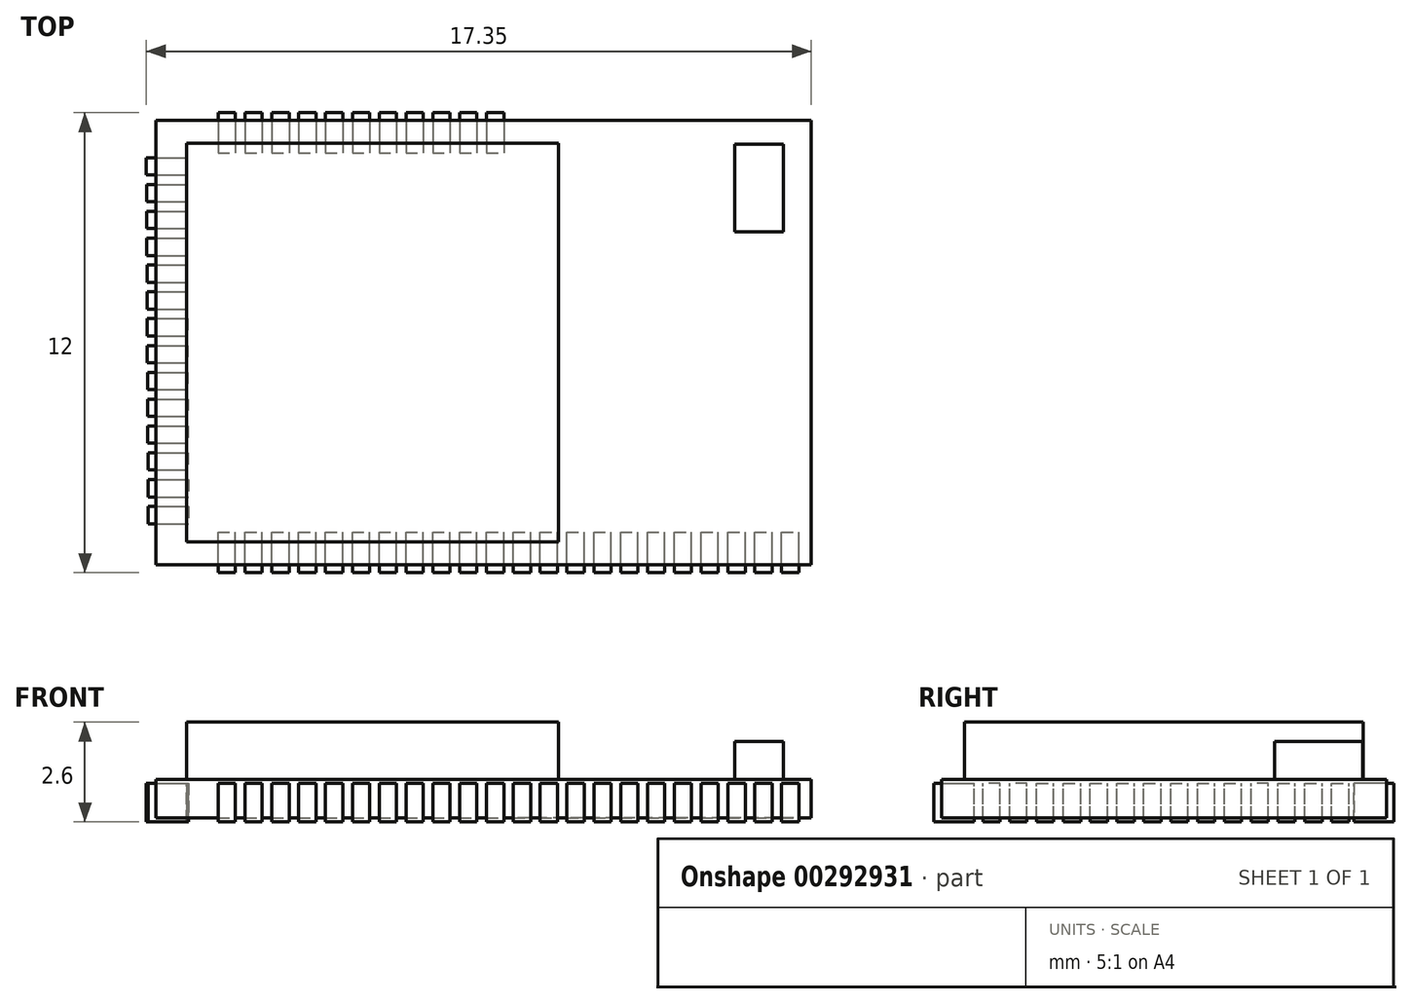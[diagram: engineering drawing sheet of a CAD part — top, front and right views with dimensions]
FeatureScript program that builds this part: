
annotation { "Feature Type Name" : "Feature", "Feature Type Description" : "" }
export const myFeature = defineFeature(function(context is Context, id is Id, definition is map)
    precondition{}
    {
        {
            var Q0;
            Q0=qCreatedBy(makeId("Top.planeOp"),FACE);
            var sketch = newSketch(context, id + "F0", { "sketchPlane" : qUnion([Q0])});
            skLineSegment(sketch, "E0.bottom", {"start": v(8.55, -5.8) * mm, "end": v(-8.55, -5.8) * mm});
            skLineSegment(sketch, "E0.top", {"start": v(8.55, 5.8) * mm, "end": v(-8.55, 5.8) * mm});
            skLineSegment(sketch, "E0.left", {"start": v(8.55, -5.8) * mm, "end": v(8.55, 5.8) * mm});
            skLineSegment(sketch, "E0.right", {"start": v(-8.55, -5.8) * mm, "end": v(-8.55, 5.8) * mm});
            skPoint(sketch, "E0.middle", {"position": v(0, 0) * mm});
            skLineSegment(sketch, "E1.bottom", {"start": v(1.95, -5.2) * mm, "end": v(-7.75, -5.2) * mm});
            skLineSegment(sketch, "E1.top", {"start": v(1.95, 5.2) * mm, "end": v(-7.75, 5.2) * mm});
            skLineSegment(sketch, "E1.left", {"start": v(1.95, -5.2) * mm, "end": v(1.95, 5.2) * mm});
            skLineSegment(sketch, "E1.right", {"start": v(-7.75, -5.2) * mm, "end": v(-7.75, 5.2) * mm});
            skPoint(sketch, "E1.middle", {"position": v(-2.9, 0) * mm});
            skLineSegment(sketch, "E2.bottom", {"start": v(7.82, 2.89) * mm, "end": v(6.55, 2.89) * mm});
            skLineSegment(sketch, "E2.top", {"start": v(7.82, 5.18) * mm, "end": v(6.55, 5.18) * mm});
            skLineSegment(sketch, "E2.left", {"start": v(7.82, 2.89) * mm, "end": v(7.82, 5.18) * mm});
            skLineSegment(sketch, "E2.right", {"start": v(6.55, 2.89) * mm, "end": v(6.55, 5.18) * mm});
            skPoint(sketch, "E2.middle", {"position": v(7.18, 4.03) * mm});
            skSolve(sketch);
        }
        {
            var Q0;
            Q0=makeQuery(id+"F0.imprint","IMPRINT",FACE,{"disambiguationData":[TD([[makeQuery(id+"F0.imprint","IMPRINT",EDGE,{"derivedFrom":sQuery(id+"F0.wireOp",EDGE,"E0.bottom")}),-1.0]])]});
            var Q1;
            Q1=makeQuery(id+"F0.imprint","IMPRINT",FACE,{"disambiguationData":[TD([[makeQuery(id+"F0.imprint","IMPRINT",EDGE,{"derivedFrom":sQuery(id+"F0.wireOp",EDGE,"E1.bottom")}),-1.0]])]});
            var Q2;
            Q2=makeQuery(id+"F0.imprint","IMPRINT",FACE,{"disambiguationData":[TD([[makeQuery(id+"F0.imprint","IMPRINT",EDGE,{"derivedFrom":sQuery(id+"F0.wireOp",EDGE,"E2.bottom")}),-1.0]])]});
            extrude(context, id + "F1", {"entities" : qUnion([Q0, Q1, Q2]), "oppositeDirection" : true, "depth" : 1 * mm});
        }
        {
            var Q0;
            Q0=makeQuery(id+"F0.imprint","IMPRINT",FACE,{"disambiguationData":[TD([[makeQuery(id+"F0.imprint","IMPRINT",EDGE,{"derivedFrom":sQuery(id+"F0.wireOp",EDGE,"E1.bottom")}),-1.0]])]});
            extrude(context, id + "F2", {"entities" : qUnion([Q0]), "depth" : 1.5 * mm});
        }
        {
            var Q0;
            Q0=makeQuery(id+"F0.imprint","IMPRINT",FACE,{"disambiguationData":[TD([[makeQuery(id+"F0.imprint","IMPRINT",EDGE,{"derivedFrom":sQuery(id+"F0.wireOp",EDGE,"E2.bottom")}),-1.0]])]});
            extrude(context, id + "F3", {"entities" : qUnion([Q0]), "depth" : 1 * mm});
        }
        {
            var Q0;
            Q0=makeQuery(id+"F1.opExtrude","CAP_FACE",FACE,{"disambiguationData":[OSD([sQuery(id+"F0.wireOp",EDGE,"E0.bottom"),sQuery(id+"F0.wireOp",EDGE,"E0.top"),sQuery(id+"F0.wireOp",EDGE,"E0.left"),sQuery(id+"F0.wireOp",EDGE,"E0.right")])],"isStart":false});
            var sketch = newSketch(context, id + "F4", { "sketchPlane" : qUnion([Q0])});
            skLineSegment(sketch, "E3.bottom", {"start": v(7.78, 6) * mm, "end": v(8.22, 6) * mm});
            skLineSegment(sketch, "E3.top", {"start": v(7.78, 4.95) * mm, "end": v(8.23, 4.95) * mm});
            skLineSegment(sketch, "E3.left", {"start": v(7.78, 6) * mm, "end": v(7.78, 4.95) * mm});
            skLineSegment(sketch, "E3.right", {"start": v(8.23, 6) * mm, "end": v(8.23, 4.95) * mm});
            skPoint(sketch, "E3.middle", {"position": v(8, 5.47) * mm});
            skPoint(sketch, "E4", {"position": v(8, 6) * mm});
            skLineSegment(sketch, "E5.1.0.0", {"start": v(7.53, 6) * mm, "end": v(7.53, 4.95) * mm});
            skLineSegment(sketch, "E5.1.0.1", {"start": v(7.08, 6) * mm, "end": v(7.08, 4.95) * mm});
            skLineSegment(sketch, "E5.1.0.2", {"start": v(7.08, 4.95) * mm, "end": v(7.53, 4.95) * mm});
            skLineSegment(sketch, "E5.1.0.3", {"start": v(7.08, 6) * mm, "end": v(7.52, 6) * mm});
            skPoint(sketch, "E5.1.0.4", {"position": v(7.3, 6) * mm});
            skPoint(sketch, "E5.1.0.5", {"position": v(7.3, 5.47) * mm});
            skLineSegment(sketch, "E5.2.0.0", {"start": v(6.83, 6) * mm, "end": v(6.83, 4.95) * mm});
            skLineSegment(sketch, "E5.2.0.1", {"start": v(6.38, 6) * mm, "end": v(6.38, 4.95) * mm});
            skLineSegment(sketch, "E5.2.0.2", {"start": v(6.38, 4.95) * mm, "end": v(6.83, 4.95) * mm});
            skLineSegment(sketch, "E5.2.0.3", {"start": v(6.38, 6) * mm, "end": v(6.82, 6) * mm});
            skPoint(sketch, "E5.2.0.4", {"position": v(6.6, 6) * mm});
            skPoint(sketch, "E5.2.0.5", {"position": v(6.6, 5.47) * mm});
            skLineSegment(sketch, "E5.3.0.0", {"start": v(6.13, 6) * mm, "end": v(6.13, 4.95) * mm});
            skLineSegment(sketch, "E5.3.0.1", {"start": v(5.68, 6) * mm, "end": v(5.68, 4.95) * mm});
            skLineSegment(sketch, "E5.3.0.2", {"start": v(5.68, 4.95) * mm, "end": v(6.13, 4.95) * mm});
            skLineSegment(sketch, "E5.3.0.3", {"start": v(5.68, 6) * mm, "end": v(6.12, 6) * mm});
            skPoint(sketch, "E5.3.0.4", {"position": v(5.9, 6) * mm});
            skPoint(sketch, "E5.3.0.5", {"position": v(5.9, 5.47) * mm});
            skLineSegment(sketch, "E5.4.0.0", {"start": v(5.43, 6) * mm, "end": v(5.43, 4.95) * mm});
            skLineSegment(sketch, "E5.4.0.1", {"start": v(4.98, 6) * mm, "end": v(4.98, 4.95) * mm});
            skLineSegment(sketch, "E5.4.0.2", {"start": v(4.98, 4.95) * mm, "end": v(5.43, 4.95) * mm});
            skLineSegment(sketch, "E5.4.0.3", {"start": v(4.98, 6) * mm, "end": v(5.42, 6) * mm});
            skPoint(sketch, "E5.4.0.4", {"position": v(5.2, 6) * mm});
            skPoint(sketch, "E5.4.0.5", {"position": v(5.2, 5.47) * mm});
            skLineSegment(sketch, "E5.5.0.0", {"start": v(4.73, 6) * mm, "end": v(4.73, 4.95) * mm});
            skLineSegment(sketch, "E5.5.0.1", {"start": v(4.28, 6) * mm, "end": v(4.28, 4.95) * mm});
            skLineSegment(sketch, "E5.5.0.2", {"start": v(4.28, 4.95) * mm, "end": v(4.73, 4.95) * mm});
            skLineSegment(sketch, "E5.5.0.3", {"start": v(4.28, 6) * mm, "end": v(4.72, 6) * mm});
            skPoint(sketch, "E5.5.0.4", {"position": v(4.5, 6) * mm});
            skPoint(sketch, "E5.5.0.5", {"position": v(4.5, 5.47) * mm});
            skLineSegment(sketch, "E5.6.0.0", {"start": v(4.03, 6) * mm, "end": v(4.03, 4.95) * mm});
            skLineSegment(sketch, "E5.6.0.1", {"start": v(3.58, 6) * mm, "end": v(3.58, 4.95) * mm});
            skLineSegment(sketch, "E5.6.0.2", {"start": v(3.58, 4.95) * mm, "end": v(4.03, 4.95) * mm});
            skLineSegment(sketch, "E5.6.0.3", {"start": v(3.58, 6) * mm, "end": v(4.02, 6) * mm});
            skPoint(sketch, "E5.6.0.4", {"position": v(3.8, 6) * mm});
            skPoint(sketch, "E5.6.0.5", {"position": v(3.8, 5.47) * mm});
            skLineSegment(sketch, "E5.7.0.0", {"start": v(3.33, 6) * mm, "end": v(3.33, 4.95) * mm});
            skLineSegment(sketch, "E5.7.0.1", {"start": v(2.88, 6) * mm, "end": v(2.88, 4.95) * mm});
            skLineSegment(sketch, "E5.7.0.2", {"start": v(2.88, 4.95) * mm, "end": v(3.33, 4.95) * mm});
            skLineSegment(sketch, "E5.7.0.3", {"start": v(2.88, 6) * mm, "end": v(3.32, 6) * mm});
            skPoint(sketch, "E5.7.0.4", {"position": v(3.1, 6) * mm});
            skPoint(sketch, "E5.7.0.5", {"position": v(3.1, 5.47) * mm});
            skLineSegment(sketch, "E5.8.0.0", {"start": v(2.63, 6) * mm, "end": v(2.63, 4.95) * mm});
            skLineSegment(sketch, "E5.8.0.1", {"start": v(2.18, 6) * mm, "end": v(2.18, 4.95) * mm});
            skLineSegment(sketch, "E5.8.0.2", {"start": v(2.18, 4.95) * mm, "end": v(2.63, 4.95) * mm});
            skLineSegment(sketch, "E5.8.0.3", {"start": v(2.18, 6) * mm, "end": v(2.62, 6) * mm});
            skPoint(sketch, "E5.8.0.4", {"position": v(2.4, 6) * mm});
            skPoint(sketch, "E5.8.0.5", {"position": v(2.4, 5.47) * mm});
            skLineSegment(sketch, "E5.9.0.0", {"start": v(1.93, 6) * mm, "end": v(1.93, 4.95) * mm});
            skLineSegment(sketch, "E5.9.0.1", {"start": v(1.48, 6) * mm, "end": v(1.48, 4.95) * mm});
            skLineSegment(sketch, "E5.9.0.2", {"start": v(1.48, 4.95) * mm, "end": v(1.93, 4.95) * mm});
            skLineSegment(sketch, "E5.9.0.3", {"start": v(1.48, 6) * mm, "end": v(1.92, 6) * mm});
            skPoint(sketch, "E5.9.0.4", {"position": v(1.7, 6) * mm});
            skPoint(sketch, "E5.9.0.5", {"position": v(1.7, 5.47) * mm});
            skLineSegment(sketch, "E5.10.0.0", {"start": v(1.23, 6) * mm, "end": v(1.23, 4.95) * mm});
            skLineSegment(sketch, "E5.10.0.1", {"start": v(0.78, 6) * mm, "end": v(0.78, 4.95) * mm});
            skLineSegment(sketch, "E5.10.0.2", {"start": v(0.78, 4.95) * mm, "end": v(1.23, 4.95) * mm});
            skLineSegment(sketch, "E5.10.0.3", {"start": v(0.78, 6) * mm, "end": v(1.22, 6) * mm});
            skPoint(sketch, "E5.10.0.4", {"position": v(1, 6) * mm});
            skPoint(sketch, "E5.10.0.5", {"position": v(1, 5.47) * mm});
            skLineSegment(sketch, "E5.11.0.0", {"start": v(0.53, 6) * mm, "end": v(0.53, 4.95) * mm});
            skLineSegment(sketch, "E5.11.0.1", {"start": v(0.08, 6) * mm, "end": v(0.08, 4.95) * mm});
            skLineSegment(sketch, "E5.11.0.2", {"start": v(0.08, 4.95) * mm, "end": v(0.53, 4.95) * mm});
            skLineSegment(sketch, "E5.11.0.3", {"start": v(0.08, 6) * mm, "end": v(0.52, 6) * mm});
            skPoint(sketch, "E5.11.0.4", {"position": v(0.3, 6) * mm});
            skPoint(sketch, "E5.11.0.5", {"position": v(0.3, 5.47) * mm});
            skLineSegment(sketch, "E5.12.0.0", {"start": v(-0.17, 6) * mm, "end": v(-0.17, 4.95) * mm});
            skLineSegment(sketch, "E5.12.0.1", {"start": v(-0.62, 6) * mm, "end": v(-0.62, 4.95) * mm});
            skLineSegment(sketch, "E5.12.0.2", {"start": v(-0.62, 4.95) * mm, "end": v(-0.17, 4.95) * mm});
            skLineSegment(sketch, "E5.12.0.3", {"start": v(-0.62, 6) * mm, "end": v(-0.18, 6) * mm});
            skPoint(sketch, "E5.12.0.4", {"position": v(-0.4, 6) * mm});
            skPoint(sketch, "E5.12.0.5", {"position": v(-0.4, 5.47) * mm});
            skLineSegment(sketch, "E5.13.0.0", {"start": v(-0.87, 6) * mm, "end": v(-0.87, 4.95) * mm});
            skLineSegment(sketch, "E5.13.0.1", {"start": v(-1.32, 6) * mm, "end": v(-1.32, 4.95) * mm});
            skLineSegment(sketch, "E5.13.0.2", {"start": v(-1.32, 4.95) * mm, "end": v(-0.87, 4.95) * mm});
            skLineSegment(sketch, "E5.13.0.3", {"start": v(-1.32, 6) * mm, "end": v(-0.88, 6) * mm});
            skPoint(sketch, "E5.13.0.4", {"position": v(-1.1, 6) * mm});
            skPoint(sketch, "E5.13.0.5", {"position": v(-1.1, 5.47) * mm});
            skLineSegment(sketch, "E5.14.0.0", {"start": v(-1.57, 6) * mm, "end": v(-1.57, 4.95) * mm});
            skLineSegment(sketch, "E5.14.0.1", {"start": v(-2.02, 6) * mm, "end": v(-2.02, 4.95) * mm});
            skLineSegment(sketch, "E5.14.0.2", {"start": v(-2.02, 4.95) * mm, "end": v(-1.57, 4.95) * mm});
            skLineSegment(sketch, "E5.14.0.3", {"start": v(-2.02, 6) * mm, "end": v(-1.58, 6) * mm});
            skPoint(sketch, "E5.14.0.4", {"position": v(-1.8, 6) * mm});
            skPoint(sketch, "E5.14.0.5", {"position": v(-1.8, 5.47) * mm});
            skLineSegment(sketch, "E5.15.0.0", {"start": v(-2.27, 6) * mm, "end": v(-2.27, 4.95) * mm});
            skLineSegment(sketch, "E5.15.0.1", {"start": v(-2.73, 6) * mm, "end": v(-2.73, 4.95) * mm});
            skLineSegment(sketch, "E5.15.0.2", {"start": v(-2.72, 4.95) * mm, "end": v(-2.28, 4.95) * mm});
            skLineSegment(sketch, "E5.15.0.3", {"start": v(-2.72, 6) * mm, "end": v(-2.28, 6) * mm});
            skPoint(sketch, "E5.15.0.4", {"position": v(-2.5, 6) * mm});
            skPoint(sketch, "E5.15.0.5", {"position": v(-2.5, 5.47) * mm});
            skLineSegment(sketch, "E5.16.0.0", {"start": v(-2.97, 6) * mm, "end": v(-2.97, 4.95) * mm});
            skLineSegment(sketch, "E5.16.0.1", {"start": v(-3.43, 6) * mm, "end": v(-3.43, 4.95) * mm});
            skLineSegment(sketch, "E5.16.0.2", {"start": v(-3.42, 4.95) * mm, "end": v(-2.98, 4.95) * mm});
            skLineSegment(sketch, "E5.16.0.3", {"start": v(-3.42, 6) * mm, "end": v(-2.98, 6) * mm});
            skPoint(sketch, "E5.16.0.4", {"position": v(-3.2, 6) * mm});
            skPoint(sketch, "E5.16.0.5", {"position": v(-3.2, 5.47) * mm});
            skLineSegment(sketch, "E5.17.0.0", {"start": v(-3.67, 6) * mm, "end": v(-3.67, 4.95) * mm});
            skLineSegment(sketch, "E5.17.0.1", {"start": v(-4.12, 6) * mm, "end": v(-4.12, 4.95) * mm});
            skLineSegment(sketch, "E5.17.0.2", {"start": v(-4.12, 4.95) * mm, "end": v(-3.67, 4.95) * mm});
            skLineSegment(sketch, "E5.17.0.3", {"start": v(-4.12, 6) * mm, "end": v(-3.68, 6) * mm});
            skPoint(sketch, "E5.17.0.4", {"position": v(-3.9, 6) * mm});
            skPoint(sketch, "E5.17.0.5", {"position": v(-3.9, 5.47) * mm});
            skLineSegment(sketch, "E5.18.0.0", {"start": v(-4.37, 6) * mm, "end": v(-4.37, 4.95) * mm});
            skLineSegment(sketch, "E5.18.0.1", {"start": v(-4.83, 6) * mm, "end": v(-4.83, 4.95) * mm});
            skLineSegment(sketch, "E5.18.0.2", {"start": v(-4.82, 4.95) * mm, "end": v(-4.38, 4.95) * mm});
            skLineSegment(sketch, "E5.18.0.3", {"start": v(-4.82, 6) * mm, "end": v(-4.38, 6) * mm});
            skPoint(sketch, "E5.18.0.4", {"position": v(-4.6, 6) * mm});
            skPoint(sketch, "E5.18.0.5", {"position": v(-4.6, 5.47) * mm});
            skLineSegment(sketch, "E5.19.0.0", {"start": v(-5.07, 6) * mm, "end": v(-5.07, 4.95) * mm});
            skLineSegment(sketch, "E5.19.0.1", {"start": v(-5.53, 6) * mm, "end": v(-5.53, 4.95) * mm});
            skLineSegment(sketch, "E5.19.0.2", {"start": v(-5.52, 4.95) * mm, "end": v(-5.08, 4.95) * mm});
            skLineSegment(sketch, "E5.19.0.3", {"start": v(-5.52, 6) * mm, "end": v(-5.08, 6) * mm});
            skPoint(sketch, "E5.19.0.4", {"position": v(-5.3, 6) * mm});
            skPoint(sketch, "E5.19.0.5", {"position": v(-5.3, 5.47) * mm});
            skLineSegment(sketch, "E5.20.0.0", {"start": v(-5.77, 6) * mm, "end": v(-5.77, 4.95) * mm});
            skLineSegment(sketch, "E5.20.0.1", {"start": v(-6.23, 6) * mm, "end": v(-6.23, 4.95) * mm});
            skLineSegment(sketch, "E5.20.0.2", {"start": v(-6.22, 4.95) * mm, "end": v(-5.78, 4.95) * mm});
            skLineSegment(sketch, "E5.20.0.3", {"start": v(-6.22, 6) * mm, "end": v(-5.78, 6) * mm});
            skPoint(sketch, "E5.20.0.4", {"position": v(-6, 6) * mm});
            skPoint(sketch, "E5.20.0.5", {"position": v(-6, 5.47) * mm});
            skLineSegment(sketch, "E5.21.0.0", {"start": v(-6.47, 6) * mm, "end": v(-6.47, 4.95) * mm});
            skLineSegment(sketch, "E5.21.0.1", {"start": v(-6.92, 6) * mm, "end": v(-6.92, 4.95) * mm});
            skLineSegment(sketch, "E5.21.0.2", {"start": v(-6.92, 4.95) * mm, "end": v(-6.47, 4.95) * mm});
            skLineSegment(sketch, "E5.21.0.3", {"start": v(-6.92, 6) * mm, "end": v(-6.48, 6) * mm});
            skPoint(sketch, "E5.21.0.4", {"position": v(-6.7, 6) * mm});
            skPoint(sketch, "E5.21.0.5", {"position": v(-6.7, 5.47) * mm});
            skLineSegment(sketch, "E5.direction1", {"start": v(7.78, 4.95) * mm, "end": v(7.08, 4.95) * mm, "construction": true});
            skLineSegment(sketch, "E6.bottom", {"start": v(-8.75, 4.27) * mm, "end": v(-7.7, 4.27) * mm});
            skLineSegment(sketch, "E6.top", {"start": v(-8.75, 4.72) * mm, "end": v(-7.7, 4.72) * mm});
            skLineSegment(sketch, "E6.left", {"start": v(-8.75, 4.27) * mm, "end": v(-8.75, 4.72) * mm});
            skLineSegment(sketch, "E6.right", {"start": v(-7.7, 4.27) * mm, "end": v(-7.7, 4.72) * mm});
            skPoint(sketch, "E6.middle", {"position": v(-8.22, 4.5) * mm});
            skPoint(sketch, "E7.0.1.0", {"position": v(-8.23, 3.8) * mm});
            skLineSegment(sketch, "E7.0.1.1", {"start": v(-8.75, 3.58) * mm, "end": v(-7.7, 3.58) * mm});
            skLineSegment(sketch, "E7.0.1.2", {"start": v(-8.75, 4.03) * mm, "end": v(-7.7, 4.03) * mm});
            skLineSegment(sketch, "E7.0.1.3", {"start": v(-7.7, 3.58) * mm, "end": v(-7.7, 4.03) * mm});
            skLineSegment(sketch, "E7.0.1.4", {"start": v(-8.75, 3.58) * mm, "end": v(-8.75, 4.03) * mm});
            skPoint(sketch, "E7.0.2.0", {"position": v(-8.23, 3.1) * mm});
            skLineSegment(sketch, "E7.0.2.1", {"start": v(-8.76, 2.88) * mm, "end": v(-7.7, 2.88) * mm});
            skLineSegment(sketch, "E7.0.2.2", {"start": v(-8.76, 3.33) * mm, "end": v(-7.7, 3.33) * mm});
            skLineSegment(sketch, "E7.0.2.3", {"start": v(-7.7, 2.88) * mm, "end": v(-7.7, 3.33) * mm});
            skLineSegment(sketch, "E7.0.2.4", {"start": v(-8.76, 2.88) * mm, "end": v(-8.76, 3.33) * mm});
            skPoint(sketch, "E7.0.3.0", {"position": v(-8.24, 2.4) * mm});
            skLineSegment(sketch, "E7.0.3.1", {"start": v(-8.76, 2.18) * mm, "end": v(-7.71, 2.18) * mm});
            skLineSegment(sketch, "E7.0.3.2", {"start": v(-8.76, 2.63) * mm, "end": v(-7.71, 2.63) * mm});
            skLineSegment(sketch, "E7.0.3.3", {"start": v(-7.71, 2.18) * mm, "end": v(-7.71, 2.63) * mm});
            skLineSegment(sketch, "E7.0.3.4", {"start": v(-8.76, 2.18) * mm, "end": v(-8.76, 2.63) * mm});
            skPoint(sketch, "E7.0.4.0", {"position": v(-8.24, 1.7) * mm});
            skLineSegment(sketch, "E7.0.4.1", {"start": v(-8.77, 1.48) * mm, "end": v(-7.72, 1.48) * mm});
            skLineSegment(sketch, "E7.0.4.2", {"start": v(-8.77, 1.93) * mm, "end": v(-7.72, 1.93) * mm});
            skLineSegment(sketch, "E7.0.4.3", {"start": v(-7.72, 1.48) * mm, "end": v(-7.72, 1.93) * mm});
            skLineSegment(sketch, "E7.0.4.4", {"start": v(-8.77, 1.48) * mm, "end": v(-8.77, 1.93) * mm});
            skPoint(sketch, "E7.0.5.0", {"position": v(-8.24, 1) * mm});
            skLineSegment(sketch, "E7.0.5.1", {"start": v(-8.77, 0.78) * mm, "end": v(-7.72, 0.78) * mm});
            skLineSegment(sketch, "E7.0.5.2", {"start": v(-8.77, 1.23) * mm, "end": v(-7.72, 1.23) * mm});
            skLineSegment(sketch, "E7.0.5.3", {"start": v(-7.72, 0.78) * mm, "end": v(-7.72, 1.23) * mm});
            skLineSegment(sketch, "E7.0.5.4", {"start": v(-8.77, 0.78) * mm, "end": v(-8.77, 1.23) * mm});
            skPoint(sketch, "E7.0.6.0", {"position": v(-8.25, 0.3) * mm});
            skLineSegment(sketch, "E7.0.6.1", {"start": v(-8.77, 0.08) * mm, "end": v(-7.72, 0.08) * mm});
            skLineSegment(sketch, "E7.0.6.2", {"start": v(-8.77, 0.53) * mm, "end": v(-7.72, 0.53) * mm});
            skLineSegment(sketch, "E7.0.6.3", {"start": v(-7.72, 0.08) * mm, "end": v(-7.72, 0.53) * mm});
            skLineSegment(sketch, "E7.0.6.4", {"start": v(-8.77, 0.08) * mm, "end": v(-8.77, 0.53) * mm});
            skPoint(sketch, "E7.0.7.0", {"position": v(-8.25, -0.4) * mm});
            skLineSegment(sketch, "E7.0.7.1", {"start": v(-8.78, -0.62) * mm, "end": v(-7.73, -0.62) * mm});
            skLineSegment(sketch, "E7.0.7.2", {"start": v(-8.78, -0.17) * mm, "end": v(-7.73, -0.17) * mm});
            skLineSegment(sketch, "E7.0.7.3", {"start": v(-7.73, -0.62) * mm, "end": v(-7.73, -0.17) * mm});
            skLineSegment(sketch, "E7.0.7.4", {"start": v(-8.78, -0.62) * mm, "end": v(-8.78, -0.17) * mm});
            skPoint(sketch, "E7.0.8.0", {"position": v(-8.26, -1.1) * mm});
            skLineSegment(sketch, "E7.0.8.1", {"start": v(-8.78, -1.32) * mm, "end": v(-7.73, -1.32) * mm});
            skLineSegment(sketch, "E7.0.8.2", {"start": v(-8.78, -0.87) * mm, "end": v(-7.73, -0.87) * mm});
            skLineSegment(sketch, "E7.0.8.3", {"start": v(-7.73, -1.32) * mm, "end": v(-7.73, -0.87) * mm});
            skLineSegment(sketch, "E7.0.8.4", {"start": v(-8.78, -1.32) * mm, "end": v(-8.78, -0.87) * mm});
            skPoint(sketch, "E7.0.9.0", {"position": v(-8.26, -1.8) * mm});
            skLineSegment(sketch, "E7.0.9.1", {"start": v(-8.78, -2.02) * mm, "end": v(-7.73, -2.02) * mm});
            skLineSegment(sketch, "E7.0.9.2", {"start": v(-8.78, -1.57) * mm, "end": v(-7.73, -1.57) * mm});
            skLineSegment(sketch, "E7.0.9.3", {"start": v(-7.73, -2.02) * mm, "end": v(-7.73, -1.57) * mm});
            skLineSegment(sketch, "E7.0.9.4", {"start": v(-8.78, -2.02) * mm, "end": v(-8.78, -1.57) * mm});
            skPoint(sketch, "E7.0.10.0", {"position": v(-8.26, -2.5) * mm});
            skLineSegment(sketch, "E7.0.10.1", {"start": v(-8.79, -2.72) * mm, "end": v(-7.74, -2.72) * mm});
            skLineSegment(sketch, "E7.0.10.2", {"start": v(-8.79, -2.27) * mm, "end": v(-7.74, -2.27) * mm});
            skLineSegment(sketch, "E7.0.10.3", {"start": v(-7.74, -2.72) * mm, "end": v(-7.74, -2.27) * mm});
            skLineSegment(sketch, "E7.0.10.4", {"start": v(-8.79, -2.72) * mm, "end": v(-8.79, -2.27) * mm});
            skPoint(sketch, "E7.0.11.0", {"position": v(-8.27, -3.2) * mm});
            skLineSegment(sketch, "E7.0.11.1", {"start": v(-8.8, -3.42) * mm, "end": v(-7.74, -3.42) * mm});
            skLineSegment(sketch, "E7.0.11.2", {"start": v(-8.8, -2.97) * mm, "end": v(-7.74, -2.97) * mm});
            skLineSegment(sketch, "E7.0.11.3", {"start": v(-7.74, -3.42) * mm, "end": v(-7.74, -2.97) * mm});
            skLineSegment(sketch, "E7.0.11.4", {"start": v(-8.8, -3.42) * mm, "end": v(-8.8, -2.97) * mm});
            skPoint(sketch, "E7.0.12.0", {"position": v(-8.27, -3.9) * mm});
            skLineSegment(sketch, "E7.0.12.1", {"start": v(-8.8, -4.12) * mm, "end": v(-7.75, -4.12) * mm});
            skLineSegment(sketch, "E7.0.12.2", {"start": v(-8.8, -3.67) * mm, "end": v(-7.75, -3.67) * mm});
            skLineSegment(sketch, "E7.0.12.3", {"start": v(-7.75, -4.12) * mm, "end": v(-7.75, -3.67) * mm});
            skLineSegment(sketch, "E7.0.12.4", {"start": v(-8.8, -4.12) * mm, "end": v(-8.8, -3.67) * mm});
            skPoint(sketch, "E7.0.13.0", {"position": v(-8.28, -4.6) * mm});
            skLineSegment(sketch, "E7.0.13.1", {"start": v(-8.8, -4.82) * mm, "end": v(-7.75, -4.82) * mm});
            skLineSegment(sketch, "E7.0.13.2", {"start": v(-8.8, -4.37) * mm, "end": v(-7.75, -4.37) * mm});
            skLineSegment(sketch, "E7.0.13.3", {"start": v(-7.75, -4.82) * mm, "end": v(-7.75, -4.37) * mm});
            skLineSegment(sketch, "E7.0.13.4", {"start": v(-8.8, -4.82) * mm, "end": v(-8.8, -4.37) * mm});
            skLineSegment(sketch, "E7.direction1", {"start": v(-8.75, 4.27) * mm, "end": v(16.25, 4.27) * mm, "construction": true});
            skLineSegment(sketch, "E7.direction2", {"start": v(-8.75, 4.27) * mm, "end": v(-8.75, 3.58) * mm, "construction": true});
            skLineSegment(sketch, "E8", {"start": v(0, 0) * mm, "end": v(-3.56, 0) * mm, "construction": true});
            skLineSegment(sketch, "E9.MirrorCS", {"start": v(-0.62, -6) * mm, "end": v(-0.18, -6) * mm});
            skLineSegment(sketch, "E10.MirrorCS", {"start": v(-6.22, -6) * mm, "end": v(-5.78, -6) * mm});
            skLineSegment(sketch, "E11.MirrorCS", {"start": v(-2.02, -6) * mm, "end": v(-1.58, -6) * mm});
            skLineSegment(sketch, "E12.MirrorCS", {"start": v(-4.82, -6) * mm, "end": v(-4.38, -6) * mm});
            skLineSegment(sketch, "E13.MirrorCS", {"start": v(-3.42, -6) * mm, "end": v(-2.98, -6) * mm});
            skLineSegment(sketch, "E14.MirrorCS", {"start": v(-2.72, -4.95) * mm, "end": v(-2.28, -4.95) * mm});
            skLineSegment(sketch, "E15.MirrorCS", {"start": v(0.08, -4.95) * mm, "end": v(0.53, -4.95) * mm});
            skLineSegment(sketch, "E16.MirrorCS", {"start": v(-5.52, -4.95) * mm, "end": v(-5.08, -4.95) * mm});
            skLineSegment(sketch, "E17.MirrorCS", {"start": v(-2.72, -6) * mm, "end": v(-2.28, -6) * mm});
            skLineSegment(sketch, "E18.MirrorCS", {"start": v(0.08, -6) * mm, "end": v(0.52, -6) * mm});
            skLineSegment(sketch, "E19.MirrorCS", {"start": v(-5.52, -6) * mm, "end": v(-5.08, -6) * mm});
            skLineSegment(sketch, "E20.MirrorCS", {"start": v(-3.42, -4.95) * mm, "end": v(-2.98, -4.95) * mm});
            skLineSegment(sketch, "E21.MirrorCS", {"start": v(-0.62, -4.95) * mm, "end": v(-0.17, -4.95) * mm});
            skLineSegment(sketch, "E22.MirrorCS", {"start": v(-6.22, -4.95) * mm, "end": v(-5.78, -4.95) * mm});
            skLineSegment(sketch, "E23.MirrorCS", {"start": v(-2.02, -4.95) * mm, "end": v(-1.57, -4.95) * mm});
            skLineSegment(sketch, "E24.MirrorCS", {"start": v(-4.82, -4.95) * mm, "end": v(-4.38, -4.95) * mm});
            skLineSegment(sketch, "E25.MirrorCS", {"start": v(-1.32, -6) * mm, "end": v(-0.88, -6) * mm});
            skLineSegment(sketch, "E26.MirrorCS", {"start": v(-6.92, -6) * mm, "end": v(-6.48, -6) * mm});
            skLineSegment(sketch, "E27.MirrorCS", {"start": v(-6.92, -4.95) * mm, "end": v(-6.47, -4.95) * mm});
            skLineSegment(sketch, "E28.MirrorCS", {"start": v(-1.32, -4.95) * mm, "end": v(-0.87, -4.95) * mm});
            skLineSegment(sketch, "E29.MirrorCS", {"start": v(0.53, -6) * mm, "end": v(0.53, -4.95) * mm});
            skLineSegment(sketch, "E30.MirrorCS", {"start": v(-5.07, -6) * mm, "end": v(-5.07, -4.95) * mm});
            skLineSegment(sketch, "E31.MirrorCS", {"start": v(-2.27, -6) * mm, "end": v(-2.27, -4.95) * mm});
            skLineSegment(sketch, "E32.MirrorCS", {"start": v(-2.97, -6) * mm, "end": v(-2.97, -4.95) * mm});
            skLineSegment(sketch, "E33.MirrorCS", {"start": v(-0.17, -6) * mm, "end": v(-0.17, -4.95) * mm});
            skLineSegment(sketch, "E34.MirrorCS", {"start": v(-5.77, -6) * mm, "end": v(-5.77, -4.95) * mm});
            skLineSegment(sketch, "E35.MirrorCS", {"start": v(-6.23, -6) * mm, "end": v(-6.23, -4.95) * mm});
            skLineSegment(sketch, "E36.MirrorCS", {"start": v(-3.43, -6) * mm, "end": v(-3.43, -4.95) * mm});
            skLineSegment(sketch, "E37.MirrorCS", {"start": v(-0.62, -6) * mm, "end": v(-0.62, -4.95) * mm});
            skLineSegment(sketch, "E38.MirrorCS", {"start": v(-5.53, -6) * mm, "end": v(-5.53, -4.95) * mm});
            skLineSegment(sketch, "E39.MirrorCS", {"start": v(0.08, -6) * mm, "end": v(0.08, -4.95) * mm});
            skLineSegment(sketch, "E40.MirrorCS", {"start": v(-2.73, -6) * mm, "end": v(-2.73, -4.95) * mm});
            skLineSegment(sketch, "E41.MirrorCS", {"start": v(-4.83, -6) * mm, "end": v(-4.83, -4.95) * mm});
            skLineSegment(sketch, "E42.MirrorCS", {"start": v(-2.02, -6) * mm, "end": v(-2.02, -4.95) * mm});
            skLineSegment(sketch, "E43.MirrorCS", {"start": v(-1.57, -6) * mm, "end": v(-1.57, -4.95) * mm});
            skLineSegment(sketch, "E44.MirrorCS", {"start": v(-4.37, -6) * mm, "end": v(-4.37, -4.95) * mm});
            skLineSegment(sketch, "E45.MirrorCS", {"start": v(-4.12, -6) * mm, "end": v(-3.68, -6) * mm});
            skLineSegment(sketch, "E46.MirrorCS", {"start": v(-6.92, -6) * mm, "end": v(-6.92, -4.95) * mm});
            skLineSegment(sketch, "E47.MirrorCS", {"start": v(-1.32, -6) * mm, "end": v(-1.32, -4.95) * mm});
            skLineSegment(sketch, "E48.MirrorCS", {"start": v(-6.47, -6) * mm, "end": v(-6.47, -4.95) * mm});
            skLineSegment(sketch, "E49.MirrorCS", {"start": v(-0.87, -6) * mm, "end": v(-0.87, -4.95) * mm});
            skLineSegment(sketch, "E50.MirrorCS", {"start": v(-3.67, -6) * mm, "end": v(-3.67, -4.95) * mm});
            skPoint(sketch, "E51.MirrorP", {"position": v(-5.3, -6) * mm});
            skPoint(sketch, "E52.MirrorP", {"position": v(0.3, -6) * mm});
            skPoint(sketch, "E53.MirrorP", {"position": v(-4.6, -6) * mm});
            skPoint(sketch, "E54.MirrorP", {"position": v(-5.3, -5.47) * mm});
            skPoint(sketch, "E55.MirrorP", {"position": v(0.3, -5.47) * mm});
            skPoint(sketch, "E56.MirrorP", {"position": v(-6, -6) * mm});
            skPoint(sketch, "E57.MirrorP", {"position": v(-0.4, -6) * mm});
            skPoint(sketch, "E58.MirrorP", {"position": v(-6, -5.47) * mm});
            skPoint(sketch, "E59.MirrorP", {"position": v(-0.4, -5.47) * mm});
            skPoint(sketch, "E60.MirrorP", {"position": v(-6.7, -6) * mm});
            skPoint(sketch, "E61.MirrorP", {"position": v(-1.1, -6) * mm});
            skPoint(sketch, "E62.MirrorP", {"position": v(-6.7, -5.47) * mm});
            skPoint(sketch, "E63.MirrorP", {"position": v(-1.1, -5.47) * mm});
            skPoint(sketch, "E64.MirrorP", {"position": v(-4.6, -5.47) * mm});
            skPoint(sketch, "E65.MirrorP", {"position": v(-3.9, -5.47) * mm});
            skPoint(sketch, "E66.MirrorP", {"position": v(-3.9, -6) * mm});
            skPoint(sketch, "E67.MirrorP", {"position": v(-3.2, -5.47) * mm});
            skPoint(sketch, "E68.MirrorP", {"position": v(-3.2, -6) * mm});
            skPoint(sketch, "E69.MirrorP", {"position": v(-2.5, -5.47) * mm});
            skLineSegment(sketch, "E70.MirrorCS", {"start": v(-4.12, -6) * mm, "end": v(-4.12, -4.95) * mm});
            skLineSegment(sketch, "E71.MirrorCS", {"start": v(-4.12, -4.95) * mm, "end": v(-3.67, -4.95) * mm});
            skPoint(sketch, "E72.MirrorP", {"position": v(-2.5, -6) * mm});
            skPoint(sketch, "E73.MirrorP", {"position": v(-1.8, -5.47) * mm});
            skPoint(sketch, "E74.MirrorP", {"position": v(-1.8, -6) * mm});
            skSolve(sketch);
        }
        {
            var Q0;
            Q0 = qSketchRegion(id + "F4", true);
            extrude(context, id + "F5", {"entities" : qUnion([Q0]), "operationType" : NewBodyOperationType.REMOVE, "oppositeDirection" : true, "depth" : 0.9 * mm});
        }
        {
            var Q0;
            Q0 = qSketchRegion(id + "F4", true);
            extrude(context, id + "F6", {"entities" : qUnion([Q0]), "depth" : 0.1 * mm, "hasSecondDirection" : true, "secondDirectionOppositeDirection" : true, "secondDirectionDepth" : 0.9 * mm});
        }
    });
